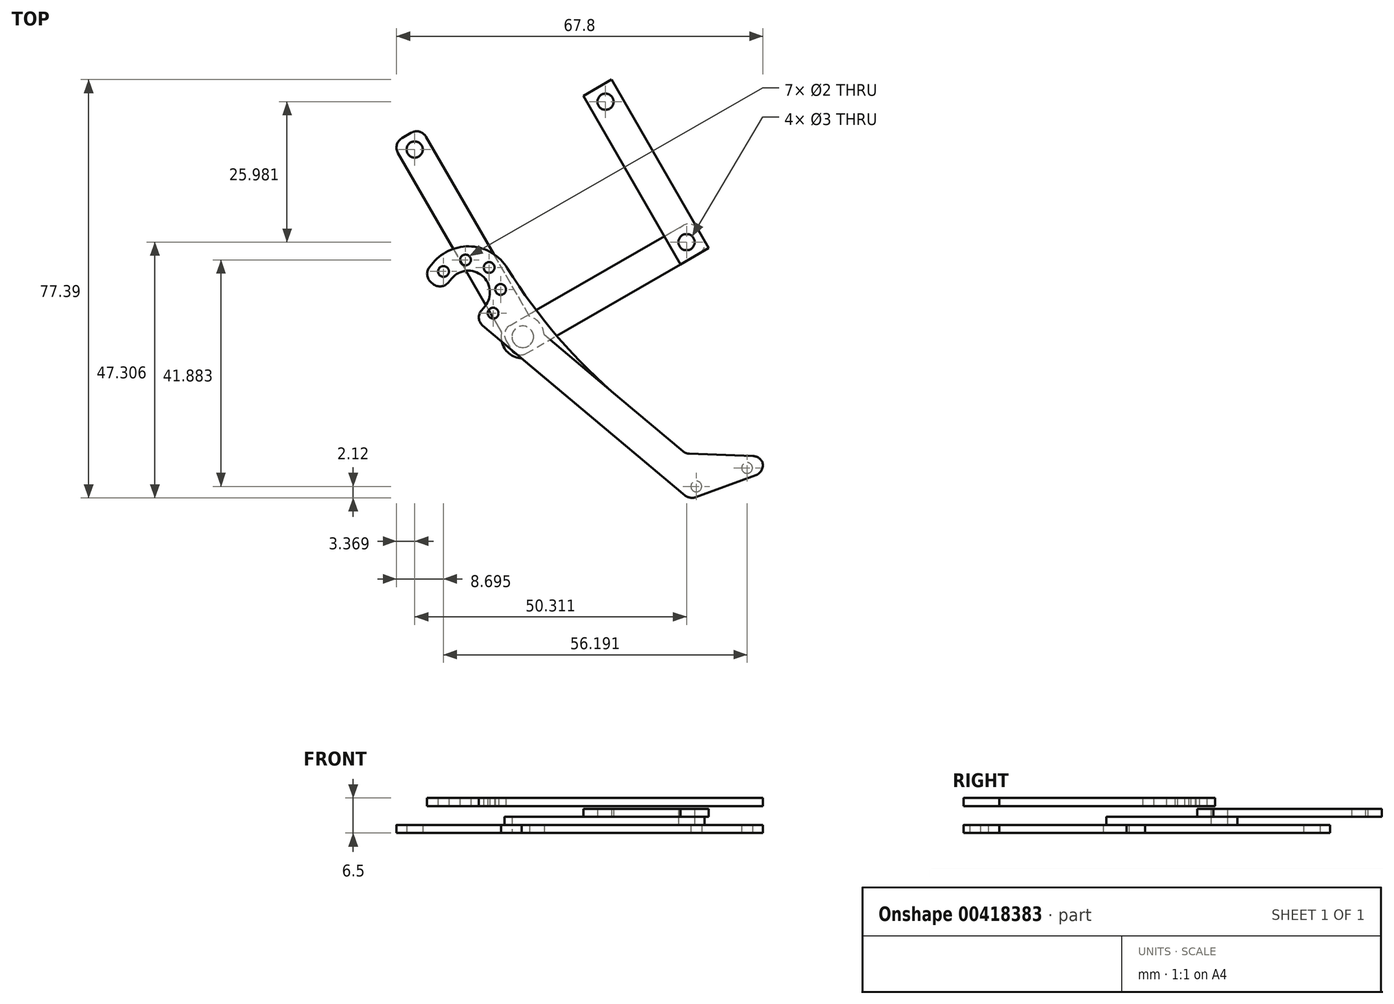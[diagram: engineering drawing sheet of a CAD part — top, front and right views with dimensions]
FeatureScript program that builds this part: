
annotation { "Feature Type Name" : "Feature", "Feature Type Description" : "" }
export const myFeature = defineFeature(function(context is Context, id is Id, definition is map)
    precondition{}
    {
        {
            var Q0;
            Q0=qCreatedBy(makeId("Top.planeOp"),FACE);
            var sketch = newSketch(context, id + "F0", { "sketchPlane" : qUnion([Q0])});
            skLineSegment(sketch, "E0", {"start": v(-22.03, 38.16) * mm, "end": v(0, 0) * mm});
            skLineSegment(sketch, "E1", {"start": v(0, 0) * mm, "end": v(25.5, -21.4) * mm});
            skLineSegment(sketch, "E2", {"start": v(32.96, -27.66) * mm, "end": v(36.82, -23.06) * mm});
            skLineSegment(sketch, "E3", {"start": v(36.82, -23.06) * mm, "end": v(4.67, 3.92) * mm});
            skLineSegment(sketch, "E4", {"start": v(4.67, 3.92) * mm, "end": v(-16.83, 41.16) * mm});
            skLineSegment(sketch, "E5", {"start": v(-16.83, 41.16) * mm, "end": v(-22.03, 38.16) * mm});
            skCircle(sketch, "E6", {"center": v(-17.93, 37.06) * mm, "radius": 1.5 * mm});
            skLineSegment(sketch, "E7", {"start": v(-19.43, 39.66) * mm, "end": v(2.07, 2.42) * mm, "construction": true});
            skLineSegment(sketch, "E8", {"start": v(2.07, 2.42) * mm, "end": v(4.67, 3.92) * mm, "construction": true});
            skLineSegment(sketch, "E9", {"start": v(2.07, 2.42) * mm, "end": v(34.9, -25.36) * mm, "construction": true});
            skCircle(sketch, "E10", {"center": v(32.6, -23.42) * mm, "radius": 1.5 * mm});
            skCircle(sketch, "E11", {"center": v(2.07, 2.42) * mm, "radius": 1.5 * mm});
            skLineSegment(sketch, "E12", {"start": v(32.6, -23.42) * mm, "end": v(9.1, -31.97) * mm, "construction": true});
            skLineSegment(sketch, "E13", {"start": v(32.96, -27.66) * mm, "end": v(10.51, -35.83) * mm});
            skLineSegment(sketch, "E14", {"start": v(10.51, -35.83) * mm, "end": v(9.1, -31.97) * mm});
            skLineSegment(sketch, "E15.MirrorCS", {"start": v(32.21, -19.2) * mm, "end": v(30.16, -19.95) * mm});
            skLineSegment(sketch, "E16.trimOffspring", {"start": v(29.33, -24.61) * mm, "end": v(32.96, -27.66) * mm});
            skLineSegment(sketch, "E17", {"start": v(25.5, -21.4) * mm, "end": v(29.33, -24.61) * mm});
            skPoint(sketch, "E18.MirrorCS.end.orphan", {"position": v(9.1, -31.97) * mm});
            skPoint(sketch, "E18.MirrorCS.start.orphan", {"position": v(7.7, -28.12) * mm});
            skLineSegment(sketch, "E19", {"start": v(25.5, -21.4) * mm, "end": v(9.1, -31.97) * mm});
            skLineSegment(sketch, "E20", {"start": v(32.96, -27.66) * mm, "end": v(47.06, -22.53) * mm});
            skLineSegment(sketch, "E21", {"start": v(47.06, -22.53) * mm, "end": v(46.03, -19.71) * mm});
            skLineSegment(sketch, "E22", {"start": v(46.03, -19.71) * mm, "end": v(32.21, -19.2) * mm});
            skSolve(sketch);
        }
        {
            var Q0;
            {var subQ1=sQuery(id+"F0.wireOp",EDGE,"E2");Q0=makeQuery(id+"F0.imprint","IMPRINT",FACE,{"disambiguationData":[TD([[makeQuery(id+"F0.imprint","IMPRINT",EDGE,{"derivedFrom":subQ1}),-1.0]])]});}
            var Q1;
            Q1=makeQuery(id+"F0.imprint","IMPRINT",FACE,{"disambiguationData":[TD([[makeQuery(id+"F0.imprint","IMPRINT",EDGE,{"derivedFrom":sQuery(id+"F0.wireOp",EDGE,"E0")}),1.0]])]});
            extrude(context, id + "F1", {"entities" : qUnion([Q0, Q1]), "depth" : 1.5 * mm});
        }
        {
            var Q0;
            Q0=makeQuery(id+"F1.opExtrude","CAP_FACE",FACE,{"disambiguationData":[OSD([sQuery(id+"F0.wireOp",EDGE,"E0"),sQuery(id+"F0.wireOp",EDGE,"E1"),sQuery(id+"F0.wireOp",EDGE,"E2"),sQuery(id+"F0.wireOp",EDGE,"E3"),sQuery(id+"F0.wireOp",EDGE,"E4"),sQuery(id+"F0.wireOp",EDGE,"E5"),sQuery(id+"F0.wireOp",EDGE,"E6"),sQuery(id+"F0.wireOp",EDGE,"E10")])],"isStart":false});
            var sketch = newSketch(context, id + "F2", { "sketchPlane" : qUnion([Q0])});
            skSolve(sketch);
        }
        {
            var Q0;
            Q0=makeQuery(id+"F2.imprint","IMPRINT",FACE,{"disambiguationData":[TD([[makeQuery(id+"F2.imprint","IMPRINT",EDGE,{"derivedFrom":makeQuery(id+"F1.opExtrude","CAP_EDGE",EDGE,{"disambiguationData":[OSD([sQuery(id+"F0.wireOp",EDGE,"E0")])],"isStart":false})}),1.0]])]});
            var sketch = newSketch(context, id + "F3", { "sketchPlane" : qUnion([Q0])});
            skLineSegment(sketch, "E23.0", {"start": v(-22.03, 38.16) * mm, "end": v(0, 0) * mm, "construction": true});
            skLineSegment(sketch, "E24.0", {"start": v(0, 0) * mm, "end": v(0, 0) * mm});
            skCircle(sketch, "E25.0", {"center": v(2.07, 2.42) * mm, "radius": 1.5 * mm});
            skLineSegment(sketch, "E26", {"start": v(2.07, 2.42) * mm, "end": v(32.38, 19.92) * mm, "construction": true});
            skCircle(sketch, "E27", {"center": v(32.38, 19.92) * mm, "radius": 1.5 * mm});
            skLineSegment(sketch, "E28", {"start": v(-2.03, 3.51) * mm, "end": v(33.48, 24.01) * mm});
            skLineSegment(sketch, "E29", {"start": v(-2.03, 3.51) * mm, "end": v(0.97, -1.68) * mm});
            skLineSegment(sketch, "E30", {"start": v(0.97, -1.68) * mm, "end": v(36.48, 18.82) * mm});
            skLineSegment(sketch, "E31", {"start": v(33.48, 24.01) * mm, "end": v(36.48, 18.82) * mm});
            skSolve(sketch);
        }
        {
            var Q0;
            Q0 = qSketchRegion(id + "F3", true);
            extrude(context, id + "F4", {"entities" : qUnion([Q0]), "depth" : 1.5 * mm});
        }
        {
            var Q0;
            Q0=makeQuery(id+"F4.opExtrude","CAP_FACE",FACE,{"disambiguationData":[OSD([sQuery(id+"F3.wireOp",EDGE,"E25.0"),sQuery(id+"F3.wireOp",EDGE,"E27"),sQuery(id+"F3.wireOp",EDGE,"E28"),sQuery(id+"F3.wireOp",EDGE,"E29"),sQuery(id+"F3.wireOp",EDGE,"E30"),sQuery(id+"F3.wireOp",EDGE,"E31")])],"isStart":false});
            var sketch = newSketch(context, id + "F5", { "sketchPlane" : qUnion([Q0])});
            skLineSegment(sketch, "E32", {"start": v(36.48, 18.82) * mm, "end": v(18.48, 50) * mm});
            skCircle(sketch, "E33.0", {"center": v(32.38, 19.92) * mm, "radius": 1.5 * mm});
            skLineSegment(sketch, "E34", {"start": v(32.38, 19.92) * mm, "end": v(17.38, 45.9) * mm, "construction": true});
            skLineSegment(sketch, "E35", {"start": v(18.48, 50) * mm, "end": v(13.28, 47) * mm});
            skLineSegment(sketch, "E36", {"start": v(13.28, 47) * mm, "end": v(31.28, 15.82) * mm});
            skCircle(sketch, "E37", {"center": v(17.38, 45.9) * mm, "radius": 1.5 * mm});
            skLineSegment(sketch, "E38", {"start": v(31.28, 15.82) * mm, "end": v(36.48, 18.82) * mm});
            skSolve(sketch);
        }
        {
            var Q0;
            Q0 = qSketchRegion(id + "F5", true);
            extrude(context, id + "F6", {"entities" : qUnion([Q0]), "depth" : 1.5 * mm});
        }
        {
            var Q0;
            Q0=makeQuery(id+"F1.opExtrude","SWEPT_EDGE",EDGE,{"disambiguationData":[OSD([sQuery(id+"F0.wireOp",EDGE,"E4"),sQuery(id+"F0.wireOp",EDGE,"E5")])]});
            var Q1;
            Q1=makeQuery(id+"F1.opExtrude","SWEPT_EDGE",EDGE,{"disambiguationData":[OSD([sQuery(id+"F0.wireOp",EDGE,"E0"),sQuery(id+"F0.wireOp",EDGE,"E5")])]});
            var Q2;
            Q2=makeQuery(id+"F4.opExtrude","SWEPT_EDGE",EDGE,{"disambiguationData":[OSD([sQuery(id+"F0.wireOp",EDGE,"E0"),sQuery(id+"F3.wireOp",EDGE,"E28"),sQuery(id+"F3.wireOp",EDGE,"E29")])]});
            var Q3;
            Q3=makeQuery(id+"F4.opExtrude","SWEPT_EDGE",EDGE,{"disambiguationData":[OSD([sQuery(id+"F3.wireOp",EDGE,"E29"),sQuery(id+"F3.wireOp",EDGE,"E30")])]});
            var Q4;
            Q4=makeQuery(id+"F4.opExtrude","SWEPT_EDGE",EDGE,{"disambiguationData":[OSD([sQuery(id+"F3.wireOp",EDGE,"E28"),sQuery(id+"F3.wireOp",EDGE,"E31")])]});
            var Q5;
            Q5=makeQuery(id+"F4.opExtrude","SWEPT_EDGE",EDGE,{"disambiguationData":[OSD([sQuery(id+"F3.wireOp",EDGE,"E30"),sQuery(id+"F3.wireOp",EDGE,"E31")])]});
            var Q6;
            Q6=makeQuery(id+"F1.opExtrude","SWEPT_EDGE",EDGE,{"disambiguationData":[OSD([sQuery(id+"F0.wireOp",EDGE,"E3"),sQuery(id+"F0.wireOp",EDGE,"E4")])]});
            var Q7;
            Q7=makeQuery(id+"F1.opExtrude","SWEPT_EDGE",EDGE,{"disambiguationData":[OSD([sQuery(id+"F0.wireOp",EDGE,"E3"),sQuery(id+"F0.wireOp",EDGE,"E22")])]});
            var Q8;
            Q8=makeQuery(id+"F1.opExtrude","SWEPT_EDGE",EDGE,{"disambiguationData":[OSD([sQuery(id+"F0.wireOp",EDGE,"E21"),sQuery(id+"F0.wireOp",EDGE,"E22")])]});
            var Q9;
            Q9=makeQuery(id+"F1.opExtrude","SWEPT_EDGE",EDGE,{"disambiguationData":[OSD([sQuery(id+"F0.wireOp",EDGE,"E20"),sQuery(id+"F0.wireOp",EDGE,"E21")])]});
            var Q10;
            Q10=makeQuery(id+"F1.opExtrude","SWEPT_EDGE",EDGE,{"disambiguationData":[OSD([sQuery(id+"F0.wireOp",EDGE,"E2"),sQuery(id+"F0.wireOp",EDGE,"E13"),sQuery(id+"F0.wireOp",EDGE,"E16.trimOffspring"),sQuery(id+"F0.wireOp",EDGE,"E20")])]});
            var Q11;
            Q11=makeQuery(id+"F1.opExtrude","SWEPT_EDGE",EDGE,{"disambiguationData":[OSD([sQuery(id+"F0.wireOp",EDGE,"E0"),sQuery(id+"F0.wireOp",EDGE,"E1")])]});
            fillet(context, id + "F7", {"entities" : qUnion([Q0, Q1, Q2, Q3, Q4, Q5, Q6, Q7, Q8, Q9, Q10, Q11]), "radius" : 2 * mm, "tangentPropagation" : true, "allowEdgeOverflow" : false});
        }
        {
            var Q0;
            Q0=makeQuery(id+"F1.opExtrude","CAP_FACE",FACE,{"disambiguationData":[OSD([sQuery(id+"F0.wireOp",EDGE,"E0"),sQuery(id+"F0.wireOp",EDGE,"E1"),sQuery(id+"F0.wireOp",EDGE,"E3"),sQuery(id+"F0.wireOp",EDGE,"E4"),sQuery(id+"F0.wireOp",EDGE,"E5"),sQuery(id+"F0.wireOp",EDGE,"E6"),sQuery(id+"F0.wireOp",EDGE,"E10"),sQuery(id+"F0.wireOp",EDGE,"E11"),sQuery(id+"F0.wireOp",EDGE,"E16.trimOffspring"),sQuery(id+"F0.wireOp",EDGE,"E17"),sQuery(id+"F0.wireOp",EDGE,"E20"),sQuery(id+"F0.wireOp",EDGE,"E21"),sQuery(id+"F0.wireOp",EDGE,"E22")])],"isStart":true});
            var sketch = newSketch(context, id + "F8", { "sketchPlane" : qUnion([Q0])});
            skCircle(sketch, "E39", {"center": v(2.07, -2.42) * mm, "radius": 4 * mm});
            skCircle(sketch, "E40", {"center": v(2.07, -2.42) * mm, "radius": 2 * mm});
            skSolve(sketch);
        }
        {
            var Q0;
            Q0 = qSketchRegion(id + "F8", true);
            extrude(context, id + "F9", {"entities" : qUnion([Q0]), "operationType" : NewBodyOperationType.ADD, "oppositeDirection" : true, "depth" : 1.5 * mm});
        }
        {
            var Q0;
            Q0=makeQuery(id+"F8.imprint","IMPRINT",FACE,{"disambiguationData":[TD([[makeQuery(id+"F8.imprint","IMPRINT",EDGE,{"derivedFrom":sQuery(id+"F8.wireOp",EDGE,"E40")}),1.0]])]});
            extrude(context, id + "F10", {"entities" : qUnion([Q0]), "operationType" : NewBodyOperationType.REMOVE, "endBound" : BoundingType.UP_TO_NEXT, "oppositeDirection" : true, "depth" : 25 * mm});
        }
        {
            var Q0;
            Q0=qCreatedBy(makeId("Top.planeOp"),FACE);
            cPlane(context, id + "F11", {"entities" : qUnion([Q0]), "cplaneType" : CPlaneType.OFFSET, "offset" : 5 * mm, "width" : 150 * mm, "height" : 150 * mm});
        }
        {
            var Q0;
            Q0=qCreatedBy(id+"F11.planeOp",FACE);
            var sketch = newSketch(context, id + "F12", { "sketchPlane" : qUnion([Q0])});
            skLineSegment(sketch, "E41.0", {"start": v(31.69, -18.76) * mm, "end": v(6.06, 2.75) * mm});
            skLineSegment(sketch, "E42.0", {"start": v(1.88, -1.58) * mm, "end": v(32.08, -26.92) * mm});
            skArc(sketch, "E43.0", {"start": v(32.9, -19.22) * mm, "mid": v(32.25, -19.1) * mm, "end": v(31.69, -18.76) * mm});
            skLineSegment(sketch, "E44.0", {"start": v(44.69, -19.66) * mm, "end": v(32.9, -19.22) * mm});
            skArc(sketch, "E45.0", {"start": v(32.08, -26.92) * mm, "mid": v(33.02, -27.36) * mm, "end": v(34.05, -27.27) * mm});
            skLineSegment(sketch, "E46.0", {"start": v(34.05, -27.27) * mm, "end": v(45.18, -23.21) * mm});
            skArc(sketch, "E47.0", {"start": v(45.18, -23.21) * mm, "mid": v(46.27, -22.26) * mm, "end": v(46.43, -20.82) * mm});
            skArc(sketch, "E48.0", {"start": v(46.43, -20.82) * mm, "mid": v(45.72, -20) * mm, "end": v(44.69, -19.66) * mm});
            skLineSegment(sketch, "E49", {"start": v(31.69, -18.76) * mm, "end": v(27.83, -23.35) * mm, "construction": true});
            skLineSegment(sketch, "E50", {"start": v(29.76, -21.05) * mm, "end": v(-8, 10.64) * mm, "construction": true});
            skCircle(sketch, "E51", {"center": v(-8, 10.64) * mm, "radius": 4 * mm});
            skLineSegment(sketch, "E52", {"start": v(-5.44, 13.7) * mm, "end": v(-10.58, 7.57) * mm, "construction": true});
            skCircle(sketch, "E53", {"center": v(-11.87, 6.04) * mm, "radius": 1 * mm, "construction": true});
            skLineSegment(sketch, "E54", {"start": v(-10.58, 7.57) * mm, "end": v(-11.87, 6.04) * mm, "construction": true});
            skCircle(sketch, "E55.1.0", {"center": v(-7.49, 4.66) * mm, "radius": 1 * mm, "construction": true});
            skCircle(sketch, "E55.2.0", {"center": v(-3.41, 6.78) * mm, "radius": 1 * mm});
            skCircle(sketch, "E55.3.0", {"center": v(-2.03, 11.16) * mm, "radius": 1 * mm});
            skCircle(sketch, "E55.4.0", {"center": v(-4.15, 15.23) * mm, "radius": 1 * mm});
            skCircle(sketch, "E55.5.0", {"center": v(-8.53, 16.61) * mm, "radius": 1 * mm});
            skCircle(sketch, "E55.6.0", {"center": v(-12.6, 14.5) * mm, "radius": 1 * mm});
            skCircle(sketch, "E55.7.0", {"center": v(-13.99, 10.11) * mm, "radius": 1 * mm, "construction": true});
            skLineSegment(sketch, "E56", {"start": v(-4.94, 8.07) * mm, "end": v(-6.87, 5.77) * mm});
            skLineSegment(sketch, "E57", {"start": v(-6.87, 5.77) * mm, "end": v(1.88, -1.58) * mm});
            skPoint(sketch, "E58", {"position": v(-4.94, 8.07) * mm});
            skLineSegment(sketch, "E59.MirrorCS", {"start": v(-11.07, 13.2) * mm, "end": v(-13, 10.9) * mm});
            skLineSegment(sketch, "E60", {"start": v(-13, 10.9) * mm, "end": v(-16.45, 13.8) * mm});
            skLineSegment(sketch, "E61", {"start": v(-16.45, 13.8) * mm, "end": v(-14.52, 16.1) * mm});
            skLineSegment(sketch, "E62", {"start": v(-14.52, 16.1) * mm, "end": v(-11.07, 13.2) * mm, "construction": true});
            skArc(sketch, "E63", {"start": v(0.01, 7.82) * mm, "mid": v(-3.8, 18.02) * mm, "end": v(-14.52, 16.1) * mm});
            skLineSegment(sketch, "E64", {"start": v(6.06, 2.75) * mm, "end": v(0.01, 7.82) * mm});
            skSolve(sketch);
        }
        {
            var Q0;
            Q0=makeQuery(id+"F12.imprint","IMPRINT",FACE,{"disambiguationData":[TD([[makeQuery(id+"F12.imprint","IMPRINT",EDGE,{"derivedFrom":sQuery(id+"F12.wireOp",EDGE,"E41.0")}),1.0]])]});
            extrude(context, id + "F13", {"entities" : qUnion([Q0]), "depth" : 1.5 * mm});
        }
        {
            var Q0;
            Q0=makeQuery(id+"F13.opExtrude","SWEPT_EDGE",EDGE,{"disambiguationData":[OSD([sQuery(id+"F12.wireOp",EDGE,"E63"),sQuery(id+"F12.wireOp",EDGE,"E64")])]});
            fillet(context, id + "F14", {"entities" : qUnion([Q0]), "radius" : 100 * mm, "tangentPropagation" : true, "allowEdgeOverflow" : false});
        }
        {
            var Q0;
            Q0=makeQuery(id+"F13.opExtrude","SWEPT_EDGE",EDGE,{"disambiguationData":[OSD([sQuery(id+"F12.wireOp",EDGE,"E60"),sQuery(id+"F12.wireOp",EDGE,"E61")])]});
            var Q1;
            Q1=makeQuery(id+"F13.opExtrude","SWEPT_EDGE",EDGE,{"disambiguationData":[OSD([sQuery(id+"F12.wireOp",EDGE,"E59.MirrorCS"),sQuery(id+"F12.wireOp",EDGE,"E60")])]});
            var Q2;
            Q2=makeQuery(id+"F13.opExtrude","SWEPT_EDGE",EDGE,{"disambiguationData":[OSD([sQuery(id+"F12.wireOp",EDGE,"E56"),sQuery(id+"F12.wireOp",EDGE,"E57")])]});
            fillet(context, id + "F15", {"entities" : qUnion([Q0, Q1, Q2]), "radius" : 2 * mm, "tangentPropagation" : true, "allowEdgeOverflow" : false});
        }
        {
            var Q0;
            Q0=makeQuery(id+"F0.imprint","IMPRINT",FACE,{"disambiguationData":[TD([[makeQuery(id+"F0.imprint","IMPRINT",EDGE,{"derivedFrom":sQuery(id+"F0.wireOp",EDGE,"E10")}),1.0]])]});
            extrude(context, id + "F16", {"entities" : qUnion([Q0]), "operationType" : NewBodyOperationType.ADD, "depth" : 1.5 * mm});
        }
        {
            var Q0;
            {var subQ0=sQuery(id+"F0.wireOp",EDGE,"E10");Q0=makeQuery(id+"F16.boolean.opBoolean","MERGE",FACE,{"derivedFrom":[makeQuery(id+"F9.boolean.opBoolean","MERGE",FACE,{"derivedFrom":[makeQuery(id+"F1.opExtrude","CAP_FACE",FACE,{"disambiguationData":[OSD([sQuery(id+"F0.wireOp",EDGE,"E0"),sQuery(id+"F0.wireOp",EDGE,"E1"),sQuery(id+"F0.wireOp",EDGE,"E3"),sQuery(id+"F0.wireOp",EDGE,"E4"),sQuery(id+"F0.wireOp",EDGE,"E5"),sQuery(id+"F0.wireOp",EDGE,"E6"),subQ0,sQuery(id+"F0.wireOp",EDGE,"E11"),sQuery(id+"F0.wireOp",EDGE,"E16.trimOffspring"),sQuery(id+"F0.wireOp",EDGE,"E17"),sQuery(id+"F0.wireOp",EDGE,"E20"),sQuery(id+"F0.wireOp",EDGE,"E21"),sQuery(id+"F0.wireOp",EDGE,"E22")])],"isStart":true}),makeQuery(id+"F9.opExtrude","CAP_FACE",FACE,{"disambiguationData":[OSD([sQuery(id+"F8.wireOp",EDGE,"E39"),sQuery(id+"F8.wireOp",EDGE,"E40")])],"isStart":true})]}),makeQuery(id+"F16.opExtrude","CAP_FACE",FACE,{"disambiguationData":[OSD([subQ0])],"isStart":true})]});}
            var sketch = newSketch(context, id + "F17", { "sketchPlane" : qUnion([Q0])});
            skLineSegment(sketch, "E65", {"start": v(46.43, 20.82) * mm, "end": v(31.35, 26.3) * mm, "construction": true});
            skCircle(sketch, "E66", {"center": v(43.59, 21.85) * mm, "radius": 1 * mm});
            skPoint(sketch, "E67", {"position": v(38.89, 23.56) * mm});
            skCircle(sketch, "E68", {"center": v(34.19, 25.27) * mm, "radius": 1 * mm});
            skSolve(sketch);
        }
        {
            var Q0;
            Q0 = qSketchRegion(id + "F17", true);
            extrude(context, id + "F18", {"entities" : qUnion([Q0]), "operationType" : NewBodyOperationType.REMOVE, "endBound" : BoundingType.UP_TO_NEXT, "oppositeDirection" : true, "depth" : 25 * mm});
        }
    });
